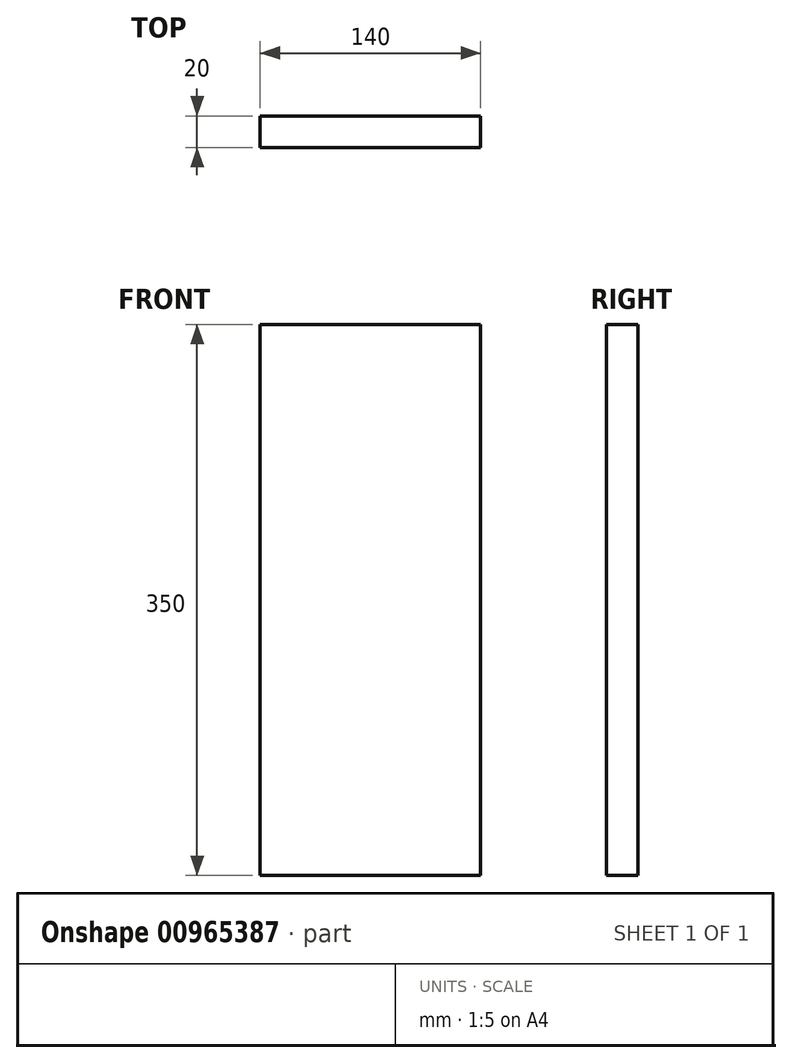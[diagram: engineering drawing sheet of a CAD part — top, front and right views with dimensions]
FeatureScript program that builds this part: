
annotation { "Feature Type Name" : "Feature", "Feature Type Description" : "" }
export const myFeature = defineFeature(function(context is Context, id is Id, definition is map)
    precondition{}
    {
        {
            var Q0;
            Q0=qCreatedBy(makeId("Top.planeOp"),FACE);
            var sketch = newSketch(context, id + "F0", { "sketchPlane" : qUnion([Q0])});
            skLineSegment(sketch, "E0.bottom", {"start": v(70, 10) * mm, "end": v(-70, 10) * mm});
            skLineSegment(sketch, "E0.top", {"start": v(70, -10) * mm, "end": v(-70, -10) * mm});
            skLineSegment(sketch, "E0.left", {"start": v(70, 10) * mm, "end": v(70, -10) * mm});
            skLineSegment(sketch, "E0.right", {"start": v(-70, 10) * mm, "end": v(-70, -10) * mm});
            skPoint(sketch, "E0.middle", {"position": v(0, 0) * mm});
            skSolve(sketch);
        }
        {
            var Q0;
            Q0=makeQuery(id+"F0.imprint","IMPRINT",FACE,{"disambiguationData":[TD([[makeQuery(id+"F0.imprint","IMPRINT",EDGE,{"derivedFrom":sQuery(id+"F0.wireOp",EDGE,"E0.bottom")}),1.0]])]});
            extrude(context, id + "F1", {"entities" : qUnion([Q0]), "depth" : 350 * mm, "offsetDistance" : 25 * mm});
        }
    });
